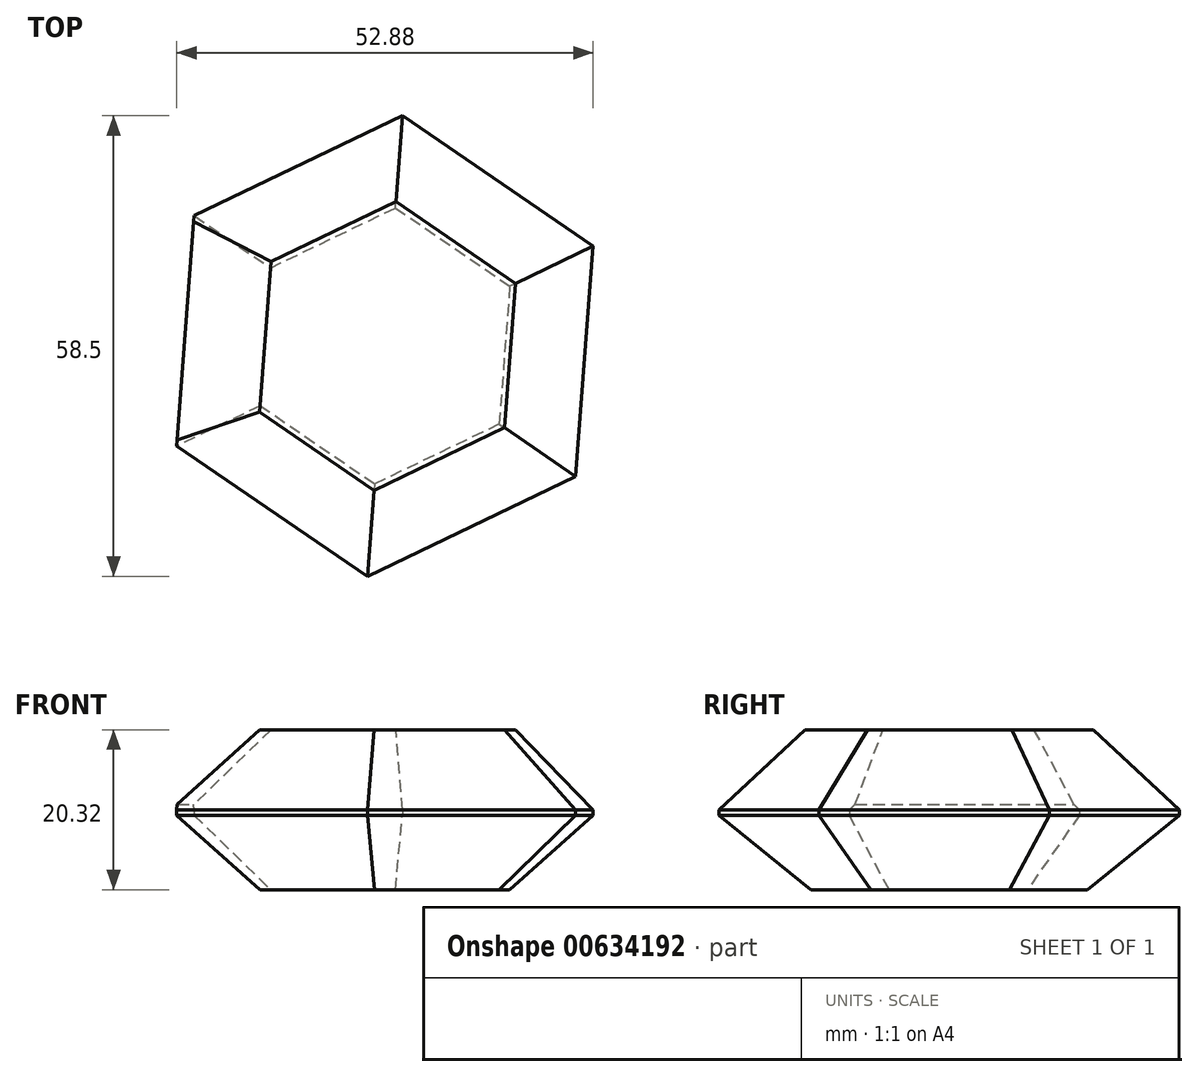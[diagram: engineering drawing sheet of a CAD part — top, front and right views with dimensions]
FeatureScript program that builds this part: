
annotation { "Feature Type Name" : "Feature", "Feature Type Description" : "" }
export const myFeature = defineFeature(function(context is Context, id is Id, definition is map)
    precondition{}
    {
        {
            var Q0;
            Q0=qCreatedBy(makeId("Top.planeOp"),FACE);
            var sketch = newSketch(context, id + "F0", { "sketchPlane" : qUnion([Q0])});
            skCircle(sketch, "E0.cCircle", {"center": v(0, 0) * mm, "radius": 25.4 * mm, "construction": true});
            skLineSegment(sketch, "E0.0", {"start": v(-26.44, -12.7) * mm, "end": v(-24.22, 16.55) * mm});
            skLineSegment(sketch, "E0.1", {"start": v(-24.22, 16.55) * mm, "end": v(2.22, 29.25) * mm});
            skLineSegment(sketch, "E0.2", {"start": v(2.22, 29.25) * mm, "end": v(26.44, 12.7) * mm});
            skLineSegment(sketch, "E0.3", {"start": v(26.44, 12.7) * mm, "end": v(24.22, -16.55) * mm});
            skLineSegment(sketch, "E0.4", {"start": v(24.22, -16.55) * mm, "end": v(-2.22, -29.25) * mm});
            skLineSegment(sketch, "E0.5", {"start": v(-2.22, -29.25) * mm, "end": v(-26.44, -12.7) * mm});
            skPoint(sketch, "E0.0.midPoint", {"position": v(-25.33, 1.93) * mm});
            skSolve(sketch);
        }
        {
            var Q0;
            Q0 = qSketchRegion(id + "F0", true);
            extrude(context, id + "F1", {"entities" : qUnion([Q0]), "endBound" : BoundingType.SYMMETRIC, "depth" : 20.32 * mm, "offsetDistance" : 25.4 * mm});
        }
        {
            var Q0;
            Q0=makeQuery(id+"F1.opExtrude","CAP_EDGE",EDGE,{"disambiguationData":[OSD([sQuery(id+"F0.wireOp",EDGE,"E0.0")])],"isStart":true});
            var Q1;
            Q1=makeQuery(id+"F1.opExtrude","CAP_EDGE",EDGE,{"disambiguationData":[OSD([sQuery(id+"F0.wireOp",EDGE,"E0.5")])],"isStart":true});
            var Q2;
            Q2=makeQuery(id+"F1.opExtrude","CAP_EDGE",EDGE,{"disambiguationData":[OSD([sQuery(id+"F0.wireOp",EDGE,"E0.4")])],"isStart":true});
            var Q3;
            Q3=makeQuery(id+"F1.opExtrude","CAP_EDGE",EDGE,{"disambiguationData":[OSD([sQuery(id+"F0.wireOp",EDGE,"E0.3")])],"isStart":true});
            var Q4;
            Q4=makeQuery(id+"F1.opExtrude","CAP_EDGE",EDGE,{"disambiguationData":[OSD([sQuery(id+"F0.wireOp",EDGE,"E0.2")])],"isStart":true});
            var Q5;
            Q5=makeQuery(id+"F1.opExtrude","CAP_EDGE",EDGE,{"disambiguationData":[OSD([sQuery(id+"F0.wireOp",EDGE,"E0.1")])],"isStart":true});
            var Q6;
            Q6=makeQuery(id+"F1.opExtrude","CAP_EDGE",EDGE,{"disambiguationData":[OSD([sQuery(id+"F0.wireOp",EDGE,"E0.0")])],"isStart":false});
            var Q7;
            Q7=makeQuery(id+"F1.opExtrude","CAP_EDGE",EDGE,{"disambiguationData":[OSD([sQuery(id+"F0.wireOp",EDGE,"E0.5")])],"isStart":false});
            var Q8;
            Q8=makeQuery(id+"F1.opExtrude","CAP_EDGE",EDGE,{"disambiguationData":[OSD([sQuery(id+"F0.wireOp",EDGE,"E0.4")])],"isStart":false});
            var Q9;
            Q9=makeQuery(id+"F1.opExtrude","CAP_EDGE",EDGE,{"disambiguationData":[OSD([sQuery(id+"F0.wireOp",EDGE,"E0.3")])],"isStart":false});
            var Q10;
            Q10=makeQuery(id+"F1.opExtrude","CAP_EDGE",EDGE,{"disambiguationData":[OSD([sQuery(id+"F0.wireOp",EDGE,"E0.2")])],"isStart":false});
            var Q11;
            Q11=makeQuery(id+"F1.opExtrude","CAP_EDGE",EDGE,{"disambiguationData":[OSD([sQuery(id+"F0.wireOp",EDGE,"E0.1")])],"isStart":false});
            chamfer(context, id + "F2", {"entities" : qUnion([Q0, Q1, Q2, Q3, Q4, Q5, Q6, Q7, Q8, Q9, Q10, Q11]), "chamferType" : ChamferType.OFFSET_ANGLE, "width" : 10.16 * mm, "oppositeDirection" : false, "angle" : 43 * degree, "tangentPropagation" : true});
        }
    });
